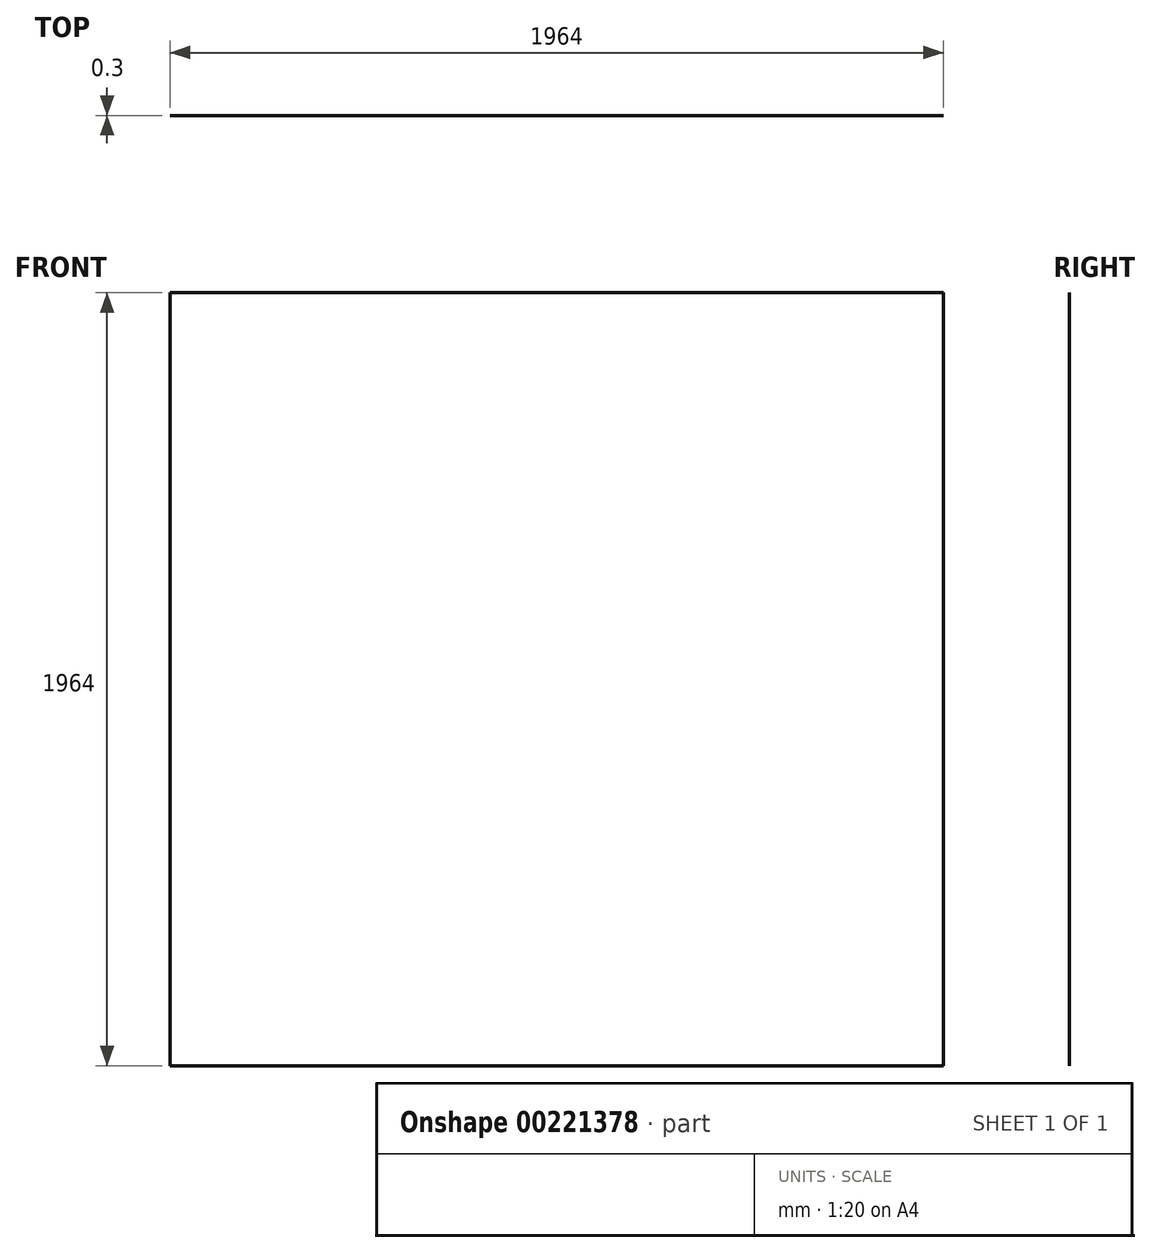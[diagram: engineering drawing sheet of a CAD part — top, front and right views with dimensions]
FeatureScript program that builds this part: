
annotation { "Feature Type Name" : "Feature", "Feature Type Description" : "" }
export const myFeature = defineFeature(function(context is Context, id is Id, definition is map)
    precondition{}
    {
        {
            var Q0;
            Q0=qCreatedBy(makeId("Front.planeOp"),FACE);
            var sketch = newSketch(context, id + "F0", { "sketchPlane" : qUnion([Q0])});
            skLineSegment(sketch, "E0.bottom", {"start": v(982, -982) * mm, "end": v(-982, -982) * mm});
            skLineSegment(sketch, "E0.top", {"start": v(982, 982) * mm, "end": v(-982, 982) * mm});
            skLineSegment(sketch, "E0.left", {"start": v(982, -982) * mm, "end": v(982, 982) * mm});
            skLineSegment(sketch, "E0.right", {"start": v(-982, -982) * mm, "end": v(-982, 982) * mm});
            skPoint(sketch, "E0.middle", {"position": v(0, 0) * mm});
            skSolve(sketch);
        }
        {
            var Q0;
            Q0=qSketchRegion(id+"F0",true);
            extrude(context, id + "F1", {"entities" : qUnion([Q0]), "depth" : 0.3 * mm});
        }
    });
